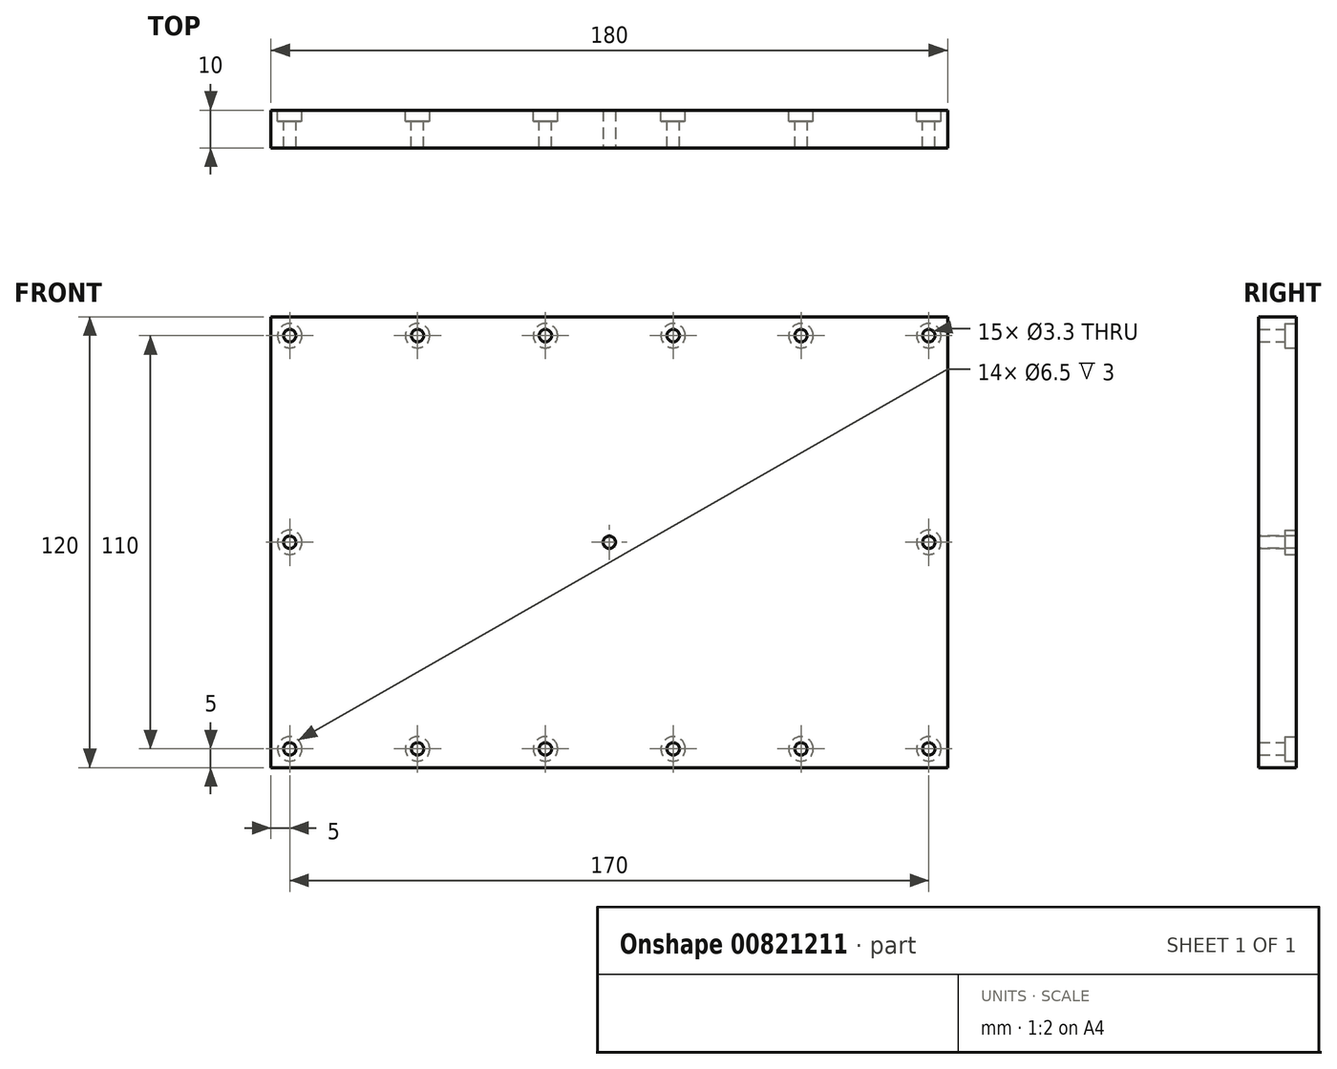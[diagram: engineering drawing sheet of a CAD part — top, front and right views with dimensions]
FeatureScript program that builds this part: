
annotation { "Feature Type Name" : "Feature", "Feature Type Description" : "" }
export const myFeature = defineFeature(function(context is Context, id is Id, definition is map)
    precondition{}
    {
        {
            var Q0;
            Q0=qCreatedBy(makeId("Front.planeOp"),FACE);
            var sketch = newSketch(context, id + "F0", { "sketchPlane" : qUnion([Q0])});
            skLineSegment(sketch, "E0.bottom", {"start": v(0, 0) * mm, "end": v(180, 0) * mm});
            skLineSegment(sketch, "E0.top", {"start": v(0, 120) * mm, "end": v(180, 120) * mm});
            skLineSegment(sketch, "E0.left", {"start": v(0, 0) * mm, "end": v(0, 120) * mm});
            skLineSegment(sketch, "E0.right", {"start": v(180, 0) * mm, "end": v(180, 120) * mm});
            skSolve(sketch);
        }
        {
            var Q0;
            Q0=makeQuery(id+"F0.imprint","IMPRINT",FACE,{"disambiguationData":[TD([[makeQuery(id+"F0.imprint","IMPRINT",EDGE,{"derivedFrom":sQuery(id+"F0.wireOp",EDGE,"E0.bottom")}),1.0]])]});
            extrude(context, id + "F1", {"entities" : qUnion([Q0]), "depth" : 10 * mm, "offsetDistance" : 25 * mm});
        }
        {
            var Q0;
            Q0=makeQuery(id+"F1.opExtrude","CAP_FACE",FACE,{"disambiguationData":[OSD([sQuery(id+"F0.wireOp",EDGE,"E0.bottom"),sQuery(id+"F0.wireOp",EDGE,"E0.top"),sQuery(id+"F0.wireOp",EDGE,"E0.left"),sQuery(id+"F0.wireOp",EDGE,"E0.right")])],"isStart":true});
            var sketch = newSketch(context, id + "F2", { "sketchPlane" : qUnion([Q0])});
            skPoint(sketch, "E1", {"position": v(-175, 115) * mm});
            skPoint(sketch, "E2", {"position": v(-165.16, 120) * mm});
            skPoint(sketch, "E3", {"position": v(-5, 115) * mm});
            skPoint(sketch, "E4", {"position": v(-5, 5) * mm});
            skPoint(sketch, "E5", {"position": v(-175, 5) * mm});
            skPoint(sketch, "E6.1.0.0", {"position": v(-141, 115) * mm});
            skPoint(sketch, "E6.2.0.0", {"position": v(-107, 115) * mm});
            skPoint(sketch, "E6.3.0.0", {"position": v(-73, 115) * mm});
            skPoint(sketch, "E6.4.0.0", {"position": v(-39, 115) * mm});
            skLineSegment(sketch, "E6.direction1", {"start": v(-175, 115) * mm, "end": v(-141, 115) * mm, "construction": true});
            skPoint(sketch, "E7.1.0.0", {"position": v(-141, 5) * mm});
            skPoint(sketch, "E7.2.0.0", {"position": v(-107, 5) * mm});
            skPoint(sketch, "E7.3.0.0", {"position": v(-73, 5) * mm});
            skPoint(sketch, "E7.4.0.0", {"position": v(-39, 5) * mm});
            skLineSegment(sketch, "E7.direction1", {"start": v(-175, 5) * mm, "end": v(-141, 5) * mm, "construction": true});
            skPoint(sketch, "E8", {"position": v(-175, 60) * mm});
            skPoint(sketch, "E9", {"position": v(-5, 60) * mm});
            skSolve(sketch);
        }
        {
            var Q0;
            Q0=sQuery(id+"F2.wireOp",VERTEX,"E1");
            var Q1;
            Q1=sQuery(id+"F2.wireOp",VERTEX,"E6.1.0.0");
            var Q2;
            Q2=sQuery(id+"F2.wireOp",VERTEX,"E6.2.0.0");
            var Q3;
            Q3=sQuery(id+"F2.wireOp",VERTEX,"E6.3.0.0");
            var Q4;
            Q4=sQuery(id+"F2.wireOp",VERTEX,"E6.4.0.0");
            var Q5;
            Q5=sQuery(id+"F2.wireOp",VERTEX,"E3");
            var Q6;
            Q6=sQuery(id+"F2.wireOp",VERTEX,"E9");
            var Q7;
            Q7=sQuery(id+"F2.wireOp",VERTEX,"E4");
            var Q8;
            Q8=sQuery(id+"F2.wireOp",VERTEX,"E7.4.0.0");
            var Q9;
            Q9=sQuery(id+"F2.wireOp",VERTEX,"E7.3.0.0");
            var Q10;
            Q10=sQuery(id+"F2.wireOp",VERTEX,"E7.2.0.0");
            var Q11;
            Q11=sQuery(id+"F2.wireOp",VERTEX,"E7.1.0.0");
            var Q12;
            Q12=sQuery(id+"F2.wireOp",VERTEX,"E8");
            var Q13;
            Q13=sQuery(id+"F2.wireOp",VERTEX,"E5");
            var Q14;
            Q14=makeQuery(id+"F1.opExtrude","SWEPT_BODY",BODY,{"disambiguationData":[OSD([sQuery(id+"F0.wireOp",EDGE,"E0.bottom"),sQuery(id+"F0.wireOp",EDGE,"E0.top"),sQuery(id+"F0.wireOp",EDGE,"E0.left"),sQuery(id+"F0.wireOp",EDGE,"E0.right")])]});
            hole(context, id + "F3", {"style" : HoleStyle.C_BORE, "endStyle" : HoleEndStyle.THROUGH, "standardTappedOrClearance" : lookupTablePath({ "standard" : "ISO", "fit" : "Normal", "size" : "M3", "type" : "Clearance" }), "standardBlindInLast" : lookupTablePath({ "fit" : "Standard", "standard" : "ISO", "size" : "M3", "type" : "Clearance" }), "holeDiameter" : 3.3 * mm, "cBoreDiameter" : 6.5 * mm, "cBoreDepth" : 3 * mm, "majorDiameter" : 5 * mm, "isTappedThrough" : true, "tappedDepth" : 18.25 * mm, "tapClearance" : 3, "locations" : qUnion([Q0, Q1, Q2, Q3, Q4, Q5, Q6, Q7, Q8, Q9, Q10, Q11, Q12, Q13]), "scope" : qUnion([Q14])});
        }
        {
            var Q0;
            Q0=makeQuery(id+"F1.opExtrude","CAP_FACE",FACE,{"disambiguationData":[OSD([sQuery(id+"F0.wireOp",EDGE,"E0.bottom"),sQuery(id+"F0.wireOp",EDGE,"E0.top"),sQuery(id+"F0.wireOp",EDGE,"E0.left"),sQuery(id+"F0.wireOp",EDGE,"E0.right")])],"isStart":false});
            var sketch = newSketch(context, id + "F4", { "sketchPlane" : qUnion([Q0])});
            skPoint(sketch, "E10", {"position": v(90, 60) * mm});
            skPoint(sketch, "E10.positionSnap0", {"position": v(90, 0) * mm});
            skPoint(sketch, "E10.positionSnap1", {"position": v(180, 60) * mm});
            skSolve(sketch);
        }
        {
            var Q0;
            Q0=sQuery(id+"F4.wireOp",VERTEX,"E10");
            var Q1;
            Q1=makeQuery(id+"F1.opExtrude","SWEPT_BODY",BODY,{"disambiguationData":[OSD([sQuery(id+"F0.wireOp",EDGE,"E0.bottom"),sQuery(id+"F0.wireOp",EDGE,"E0.top"),sQuery(id+"F0.wireOp",EDGE,"E0.left"),sQuery(id+"F0.wireOp",EDGE,"E0.right")])]});
            hole(context, id + "F5", {"style" : HoleStyle.SIMPLE, "endStyle" : HoleEndStyle.THROUGH, "standardTappedOrClearance" : lookupTablePath({ "standard" : "ISO", "fit" : "Normal", "size" : "M3", "type" : "Clearance" }), "standardBlindInLast" : lookupTablePath({ "fit" : "Standard", "standard" : "ISO", "size" : "M3", "type" : "Clearance" }), "holeDiameter" : 3.3 * mm, "majorDiameter" : 5 * mm, "isTappedThrough" : true, "tappedDepth" : 18.25 * mm, "tapClearance" : 3, "locations" : qUnion([Q0]), "scope" : qUnion([Q1])});
        }
    });
